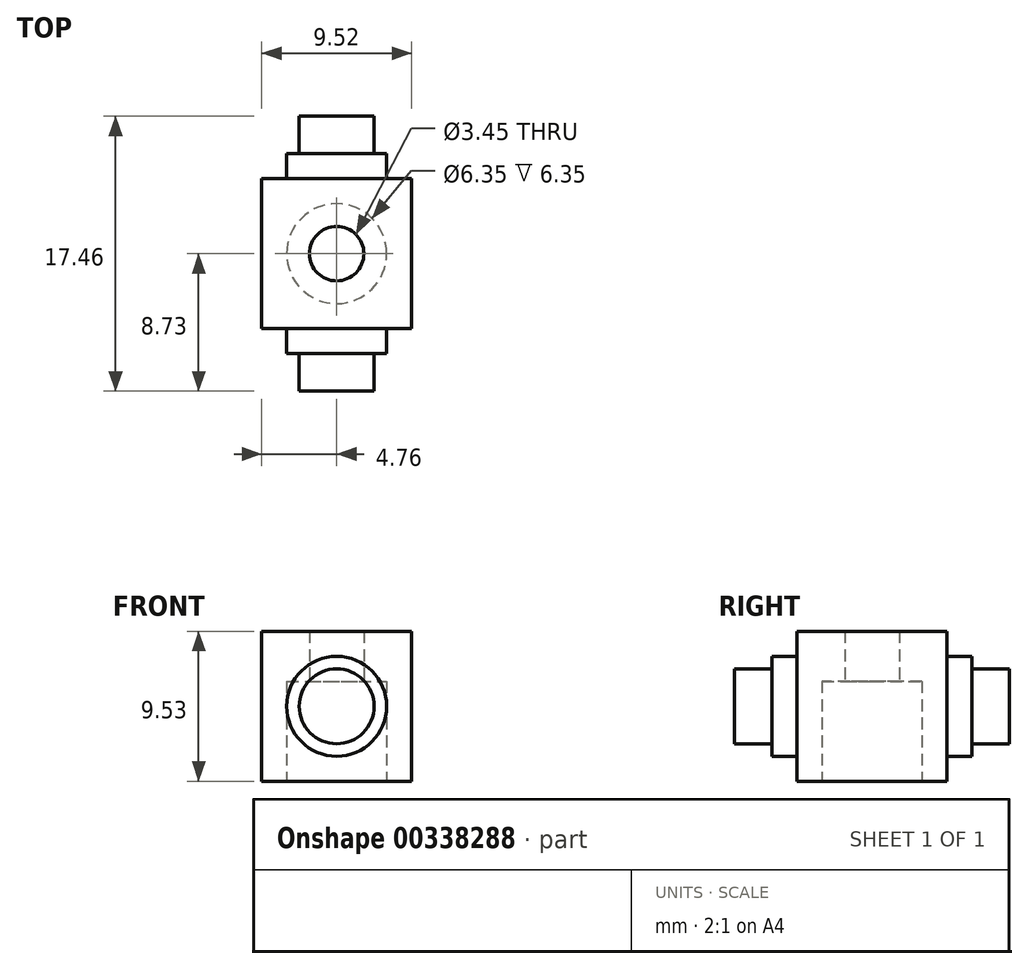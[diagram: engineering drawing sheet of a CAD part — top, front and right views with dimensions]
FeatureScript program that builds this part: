
annotation { "Feature Type Name" : "Feature", "Feature Type Description" : "" }
export const myFeature = defineFeature(function(context is Context, id is Id, definition is map)
    precondition{}
    {
        {
            var Q0;
            Q0=qCreatedBy(makeId("Top.planeOp"),FACE);
            var sketch = newSketch(context, id + "F0", { "sketchPlane" : qUnion([Q0])});
            skLineSegment(sketch, "E0.bottom", {"start": v(4.76, 4.76) * mm, "end": v(-4.76, 4.76) * mm});
            skLineSegment(sketch, "E0.top", {"start": v(4.76, -4.76) * mm, "end": v(-4.76, -4.76) * mm});
            skLineSegment(sketch, "E0.left", {"start": v(4.76, 4.76) * mm, "end": v(4.76, -4.76) * mm});
            skLineSegment(sketch, "E0.right", {"start": v(-4.76, 4.76) * mm, "end": v(-4.76, -4.76) * mm});
            skPoint(sketch, "E0.middle", {"position": v(0, 0) * mm});
            skSolve(sketch);
        }
        {
            var Q0;
            Q0 = qSketchRegion(id + "F0", true);
            extrude(context, id + "F1", {"entities" : qUnion([Q0]), "depth" : 9.52 * mm});
        }
        {
            var Q0;
            Q0=qCreatedBy(makeId("Front.planeOp"),FACE);
            var sketch = newSketch(context, id + "F2", { "sketchPlane" : qUnion([Q0])});
            skCircle(sketch, "E1", {"center": v(0, 4.76) * mm, "radius": 3.18 * mm});
            skLineSegment(sketch, "E2", {"start": v(0, 0) * mm, "end": v(0, 9.53) * mm, "construction": true});
            skSolve(sketch);
        }
        {
            var Q0;
            Q0 = qSketchRegion(id + "F2", true);
            extrude(context, id + "F3", {"entities" : qUnion([Q0]), "operationType" : NewBodyOperationType.ADD, "depth" : 12.7 * mm, "symmetric" : true});
        }
        {
            var Q0;
            Q0=qCreatedBy(makeId("Front.planeOp"),FACE);
            var sketch = newSketch(context, id + "F4", { "sketchPlane" : qUnion([Q0])});
            skCircle(sketch, "E3", {"center": v(0, 4.76) * mm, "radius": 2.38 * mm});
            skSolve(sketch);
        }
        {
            var Q0;
            Q0 = qSketchRegion(id + "F4", true);
            extrude(context, id + "F5", {"entities" : qUnion([Q0]), "operationType" : NewBodyOperationType.ADD, "depth" : 17.46 * mm, "symmetric" : true});
        }
        {
            var Q0;
            Q0=makeQuery(id+"F1.opExtrude","CAP_FACE",FACE,{"disambiguationData":[OSD([sQuery(id+"F0.wireOp",EDGE,"E0.bottom"),sQuery(id+"F0.wireOp",EDGE,"E0.top"),sQuery(id+"F0.wireOp",EDGE,"E0.left"),sQuery(id+"F0.wireOp",EDGE,"E0.right")])],"isStart":true});
            var sketch = newSketch(context, id + "F6", { "sketchPlane" : qUnion([Q0])});
            skCircle(sketch, "E4", {"center": v(0, 0) * mm, "radius": 1.73 * mm});
            skSolve(sketch);
        }
        {
            var Q0;
            Q0 = qSketchRegion(id + "F6", true);
            var Q1;
            Q1=makeQuery(id+"F1.opExtrude","CAP_FACE",FACE,{"disambiguationData":[OSD([sQuery(id+"F0.wireOp",EDGE,"E0.bottom"),sQuery(id+"F0.wireOp",EDGE,"E0.top"),sQuery(id+"F0.wireOp",EDGE,"E0.left"),sQuery(id+"F0.wireOp",EDGE,"E0.right")])],"isStart":false});
            extrude(context, id + "F7", {"entities" : qUnion([Q0]), "operationType" : NewBodyOperationType.REMOVE, "endBound" : BoundingType.UP_TO_SURFACE, "oppositeDirection" : true, "endBoundEntityFace" : qUnion([Q1]), "depth" : 25.4 * mm});
        }
        {
            var Q0;
            Q0=makeQuery(id+"F1.opExtrude","CAP_FACE",FACE,{"disambiguationData":[OSD([sQuery(id+"F0.wireOp",EDGE,"E0.bottom"),sQuery(id+"F0.wireOp",EDGE,"E0.top"),sQuery(id+"F0.wireOp",EDGE,"E0.left"),sQuery(id+"F0.wireOp",EDGE,"E0.right")])],"isStart":true});
            var sketch = newSketch(context, id + "F8", { "sketchPlane" : qUnion([Q0])});
            skCircle(sketch, "E5", {"center": v(0, 0) * mm, "radius": 3.18 * mm});
            skSolve(sketch);
        }
        {
            var Q0;
            Q0 = qSketchRegion(id + "F8", true);
            extrude(context, id + "F9", {"entities" : qUnion([Q0]), "operationType" : NewBodyOperationType.REMOVE, "oppositeDirection" : true, "depth" : 6.35 * mm});
        }
    });
